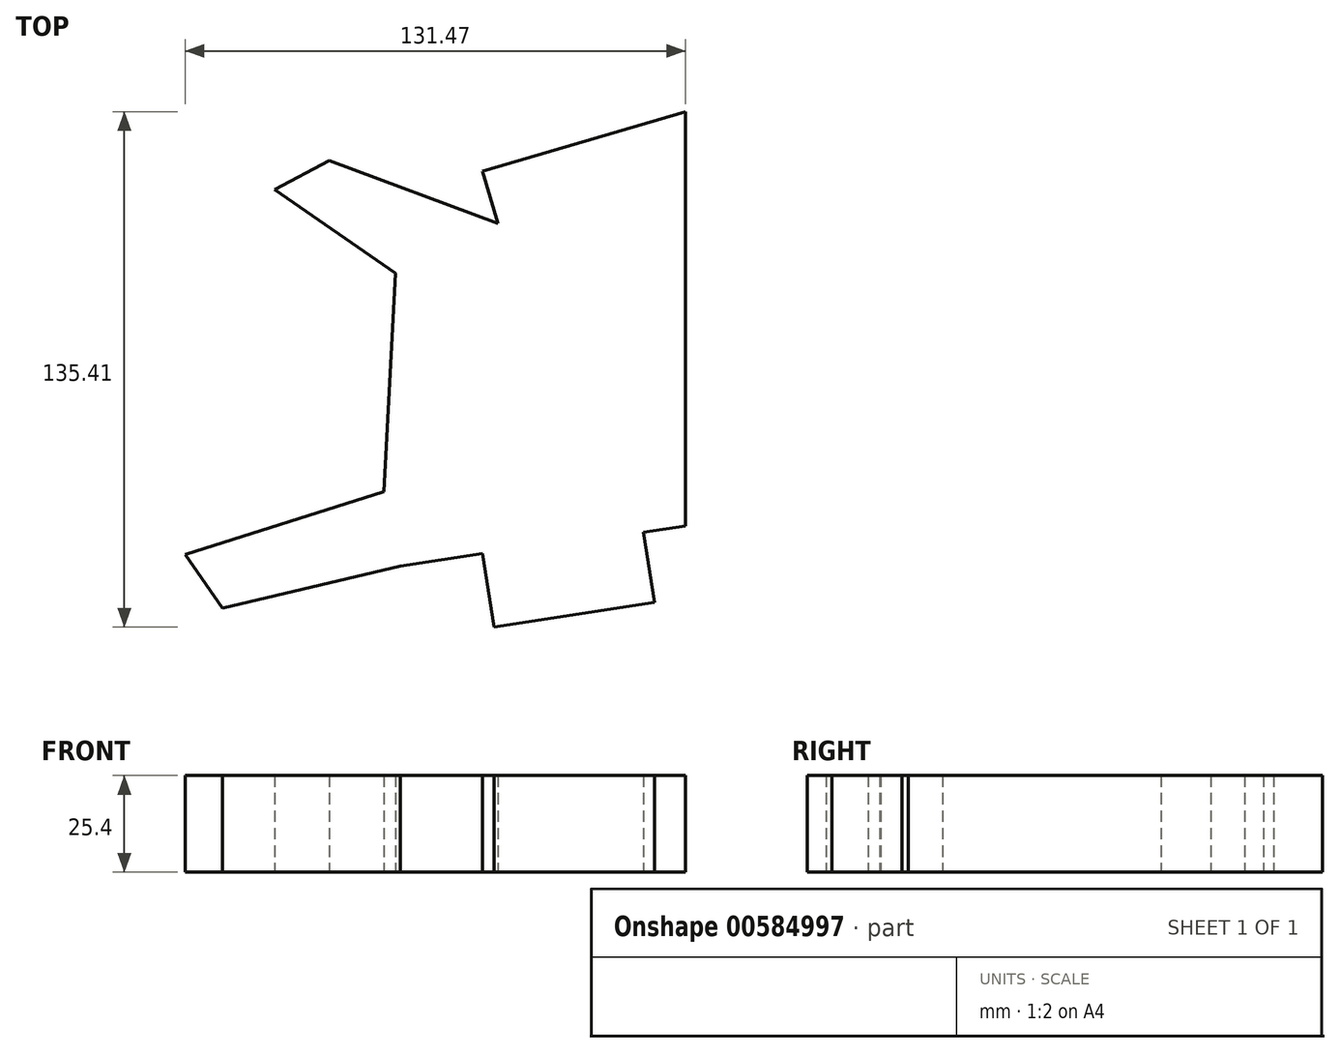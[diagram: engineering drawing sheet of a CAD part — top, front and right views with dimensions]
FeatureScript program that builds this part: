
annotation { "Feature Type Name" : "Feature", "Feature Type Description" : "" }
export const myFeature = defineFeature(function(context is Context, id is Id, definition is map)
    precondition{}
    {
        {
            var Q0;
            Q0=qCreatedBy(makeId("Top.planeOp"),FACE);
            var sketch = newSketch(context, id + "F0", { "sketchPlane" : qUnion([Q0])});
            skLineSegment(sketch, "E0", {"start": v(0, 65.8) * mm, "end": v(-53.29, 50.24) * mm});
            skLineSegment(sketch, "E1", {"start": v(-53.29, 50.24) * mm, "end": v(-49.25, 36.42) * mm});
            skLineSegment(sketch, "E2", {"start": v(-49.25, 36.42) * mm, "end": v(-93.6, 52.98) * mm});
            skLineSegment(sketch, "E3", {"start": v(-93.6, 52.98) * mm, "end": v(-107.95, 45.35) * mm});
            skLineSegment(sketch, "E4", {"start": v(-107.95, 45.35) * mm, "end": v(-76.2, 23.36) * mm});
            skLineSegment(sketch, "E5", {"start": v(-76.2, 23.36) * mm, "end": v(-79.25, -34.05) * mm});
            skLineSegment(sketch, "E6", {"start": v(-79.25, -34.05) * mm, "end": v(-131.47, -50.54) * mm});
            skLineSegment(sketch, "E7", {"start": v(-131.47, -50.54) * mm, "end": v(-121.7, -64.59) * mm});
            skLineSegment(sketch, "E8", {"start": v(-121.7, -64.59) * mm, "end": v(-74.97, -53.6) * mm});
            skLineSegment(sketch, "E9", {"start": v(-74.97, -53.6) * mm, "end": v(-53.29, -50.24) * mm});
            skLineSegment(sketch, "E10", {"start": v(-53.29, -50.24) * mm, "end": v(-50.29, -69.6) * mm});
            skLineSegment(sketch, "E11", {"start": v(-50.29, -69.6) * mm, "end": v(-8.16, -63.07) * mm});
            skLineSegment(sketch, "E12", {"start": v(-8.16, -63.07) * mm, "end": v(-11, -44.72) * mm});
            skLineSegment(sketch, "E13", {"start": v(-11, -44.72) * mm, "end": v(0, -43.01) * mm});
            skLineSegment(sketch, "E14", {"start": v(0, -43.01) * mm, "end": v(0, 65.8) * mm});
            skSolve(sketch);
        }
        {
            var Q0;
            Q0 = qSketchRegion(id + "F0", true);
            extrude(context, id + "F1", {"entities" : qUnion([Q0]), "depth" : 25.4 * mm, "offsetDistance" : 25.4 * mm});
        }
    });
